# Revit family: Domotics-DomesticRanges-GEWISS-CHORUS_DATA-SOCKET-OUTLET_TV_2M
name_source: partatom
category: Apparecchi elettrici
revit_build: Autodesk Revit 2016 (Build: 20161004_0715(x64)
units: mm (PartAtom-declared; Revit-internal decimal feet)

## family parameters
Condiviso = Sì
Host = Superficie
Mantenere orientamento annotazione = Sì
Punto di calcolo locali = Sì
Quota connettore circolare = Usa diametro
Taglio con vuoti quando caricato = Sì
Tipo di parte = Normale

## types (3) — shared parameters
Carico apparente = 0 VA
Catalogue = DOMOTICS
Catalogue Range = CHORUS - DOMESTIC RANGE
Electrocod = 3722
IDF = 4883c98a-1aa9-4cba-8233-40c92f23e849
IDT = f89402ba-8240-4a2e-bb08-6181f0328f02
Immagine tipo = GW14367.jpg
N. poli = 1
Produttore = GEWISS S.p.A.
Prospetto di default = 1219 mm
Technical sheet = https://www.gewiss.com
Tipo_ = SYSTEM PRESE TV_GENERICO : GW14361
URL = https://www.gewiss.com
Version file RFA = 19.0
Volt = 230 V

## per-type parameters (varying)
| type | Descrizione | EAN code | Modello |
| GW12367 - TV SOCKET 2M DIR. MALE CONN 9.5mm B | TV SOCKET 2M DIR. MALE CONN 9.5mm B | 8011564823716 | GW12367 |
| GW10367 - TV SOCKET 2M DIR. MALE CONN 9.5mm W | TV SOCKET 2M DIR. MALE CONN 9.5mm W | 8011564823648 | GW10367 |
| GW14367 - TV SOCKET 2M DIR. MALE CONN 9.5mm T | TV SOCKET 2M DIR. MALE CONN 9.5mm T | 8011564823723 | GW14367 |

## geometry (parser evidence)
native form markers: Sweep x1
no freeform markers — native parametric forms only
